# Revit family: Deca_Monocomando Lavatório Unic_2875.C90_Mesa Bica Baixa
name_source: partatom
category: Plumbing Fixtures
revit_build: Autodesk Revit Architecture 2012 (Build: 20120126_0600(x64)
units: mm (PartAtom-declared; Revit-internal decimal feet)

## types (3) — shared parameters
Acompanha o Produto = Ligação Flexível
Aprovado por = Contino/quattroD
Assembly Code = D2020
Atendimento ao Cliente = 0800-0117073
Consumo = Varia com a pressão
Criado por = Contino/quattroD
Description = Monocomando lavatório
Diâmetro Água Fria = 15 mm  [stored 0.0492126 ft]
Diâmetro Água Quente = 15 mm  [stored 0.0492126 ft]
Flow Pressure = 0.00 psi
Informações Complementares = Mecanismo: Monocomando
Linha = Unic
Louça/Metais = Metal
Manufacturer = Deca
Material = Deca_Latão Cromado e Plástico de Engenharia
Norma = ABNT NBR 15267: 2005
Peso Liquido (Kg) = 1.53
Pressão = 2 A 40 mca
Produto = Monocomando lavatório mesa bica baixa Unic
Raio Água Fria = 8 mm  [stored 0.0262467 ft]
Raio Água Quente = 8 mm  [stored 0.0262467 ft]
Segmento = Luxo
URL = www.deca.com.br/produtos
Variações de COR = Cromado (2875.C90), Preto Fosco (2875.F90.PTO); Gold (2875.D90.GLD).
zero-valued in all types: CWFU, Default Elevation, HWFU, WFU

## per-type parameters (varying)
| type | Código | Model | Monocomando |
| 2875.C90_Cromado CR10 | 2875.C90 | 2875.C90 | Deca CR10 Cromado Metal |
| 2875.D90.GLD_Gold GLD | 2875.D90.GLD | 2875.D90.GLD | Deca GLD Gold Metal |
| 2875.F90.PTO_Preto Fosco PR15 | 2875.F90.PTO | 2875.F90.PTO | Deca PR15 Preto Fosco Metal |

note: [stored X ft] marks values corroborated as IEEE doubles in the binary element streams (Revit-internal decimal feet)

## geometry (parser evidence)
native form markers: Blend x4, Sweep x1
no freeform markers — native parametric forms only
